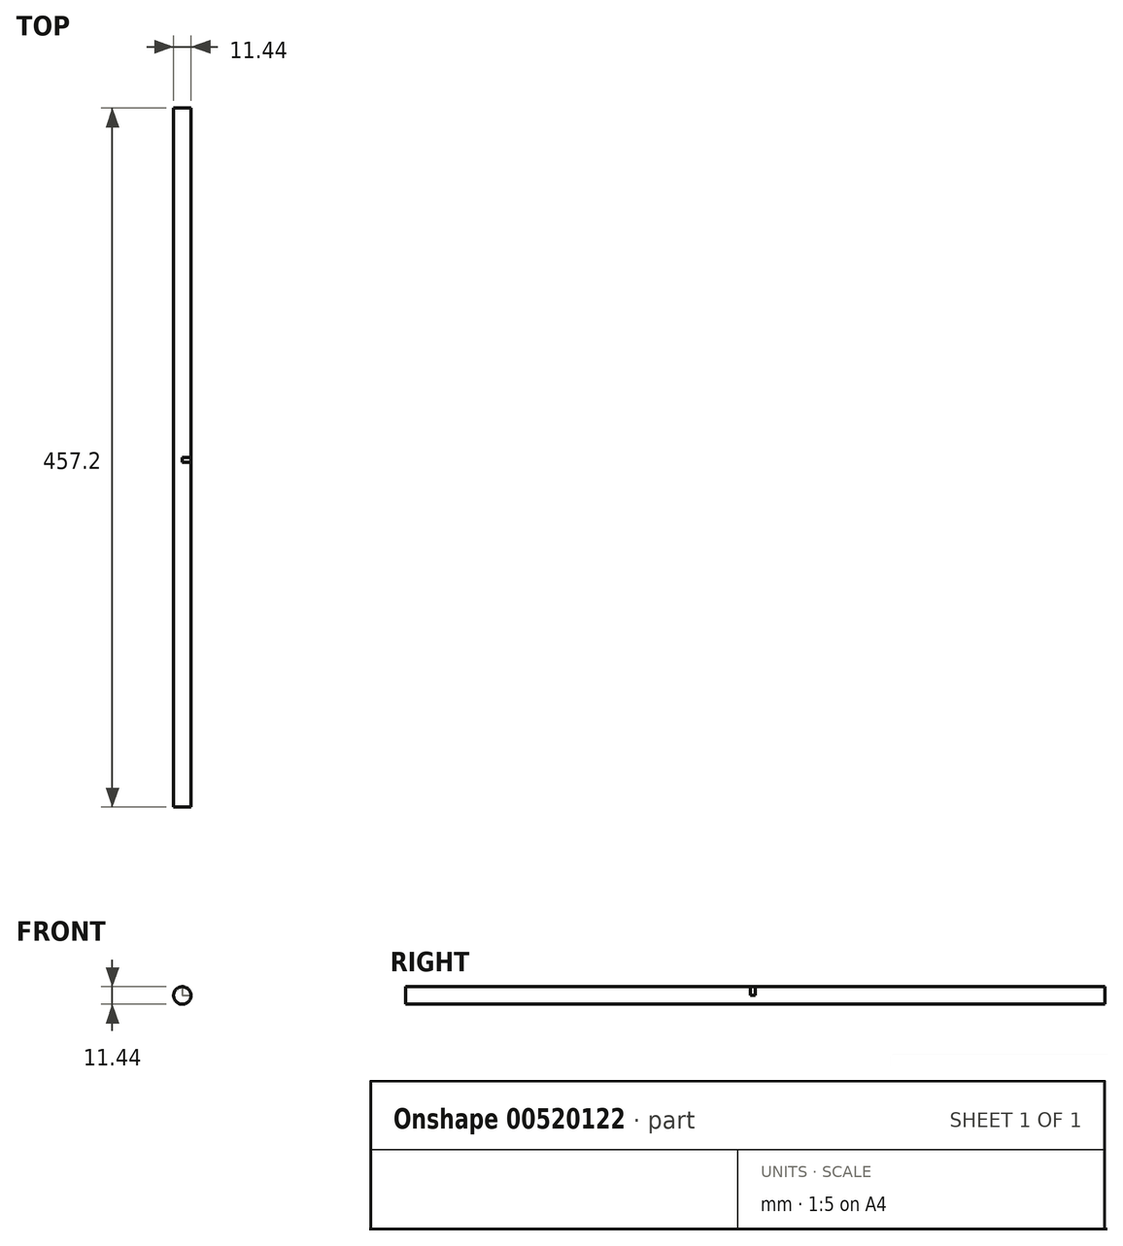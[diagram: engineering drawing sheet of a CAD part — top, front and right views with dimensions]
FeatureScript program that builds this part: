
annotation { "Feature Type Name" : "Feature", "Feature Type Description" : "" }
export const myFeature = defineFeature(function(context is Context, id is Id, definition is map)
    precondition{}
    {
        {
            var Q0;
            Q0=qCreatedBy(makeId("Front.planeOp"),FACE);
            var sketch = newSketch(context, id + "F0", { "sketchPlane" : qUnion([Q0])});
            skCircle(sketch, "E0", {"center": v(0, 0) * mm, "radius": 5.72 * mm});
            skSolve(sketch);
        }
        {
            var Q0;
            Q0=makeQuery(id+"F0.imprint","IMPRINT",FACE,{"disambiguationData":[TD([[makeQuery(id+"F0.imprint","IMPRINT",EDGE,{"derivedFrom":sQuery(id+"F0.wireOp",EDGE,"E0")}),1.0]])]});
            extrude(context, id + "F1", {"entities" : qUnion([Q0]), "depth" : 457.2 * mm, "offsetDistance" : 25.4 * mm});
        }
        {
            var Q0;
            Q0=qCreatedBy(makeId("Top.planeOp"),FACE);
            var sketch = newSketch(context, id + "F2", { "sketchPlane" : qUnion([Q0])});
            skLineSegment(sketch, "E1", {"start": v(0, -231.78) * mm, "end": v(6.35, -231.78) * mm});
            skLineSegment(sketch, "E2", {"start": v(6.35, -231.78) * mm, "end": v(6.35, -228.6) * mm});
            skLineSegment(sketch, "E3", {"start": v(6.35, -228.6) * mm, "end": v(0, -228.6) * mm});
            skLineSegment(sketch, "E4", {"start": v(0, -228.6) * mm, "end": v(0, -231.78) * mm});
            skSolve(sketch);
        }
        {
            var Q0;
            Q0 = qSketchRegion(id + "F2", true);
            extrude(context, id + "F3", {"entities" : qUnion([Q0]), "operationType" : NewBodyOperationType.REMOVE, "endBound" : BoundingType.THROUGH_ALL, "depth" : 5.08 * mm, "offsetDistance" : 25.4 * mm});
        }
    });
